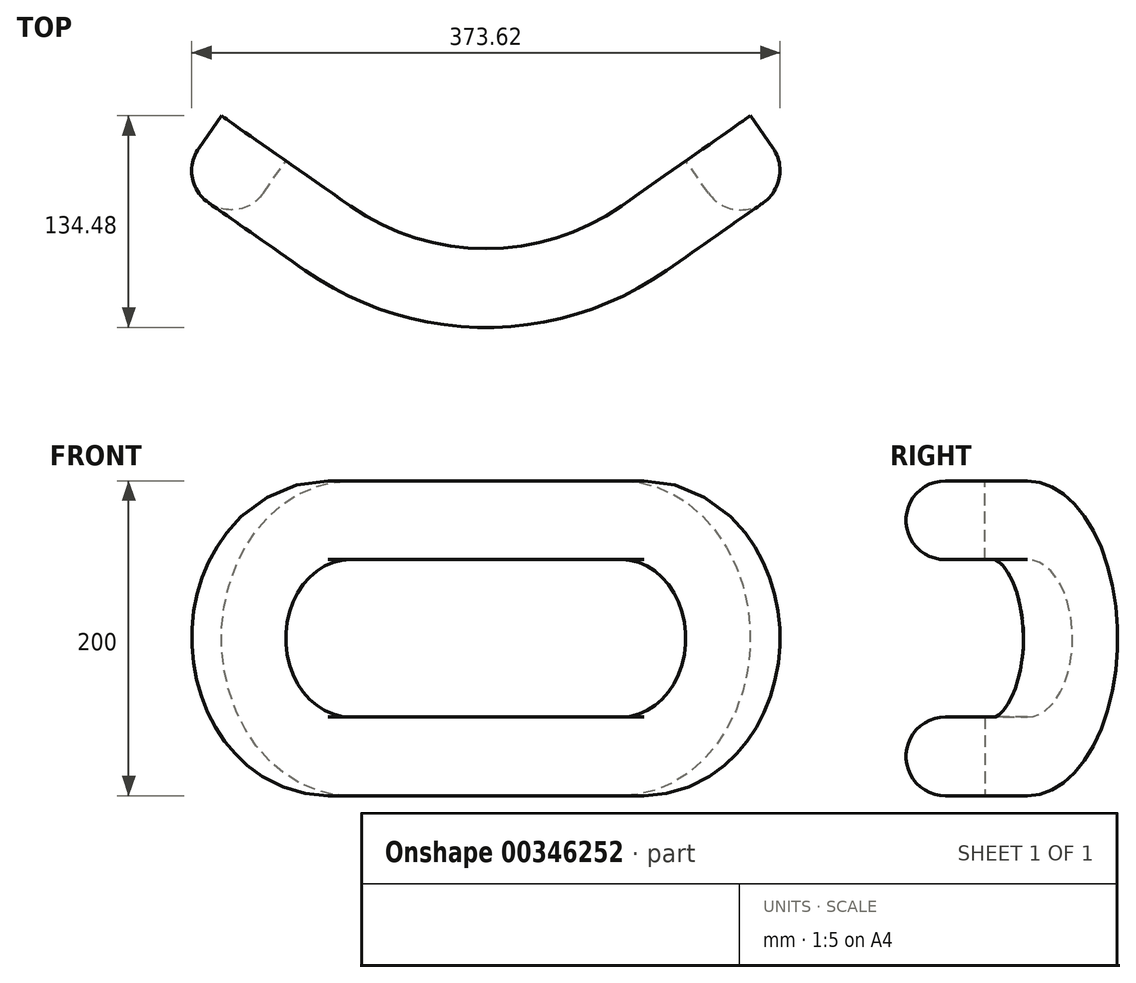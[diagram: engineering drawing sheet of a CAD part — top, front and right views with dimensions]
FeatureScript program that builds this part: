
annotation { "Feature Type Name" : "Feature", "Feature Type Description" : "" }
export const myFeature = defineFeature(function(context is Context, id is Id, definition is map)
    precondition{}
    {
        {
            var Q0;
            Q0=qCreatedBy(makeId("Top.planeOp"),FACE);
            var sketch = newSketch(context, id + "F0", { "sketchPlane" : qUnion([Q0])});
            skArc(sketch, "E0", {"start": v(-86.04, -122.87) * mm, "mid": v(0, -150) * mm, "end": v(86.04, -122.87) * mm});
            skLineSegment(sketch, "E1", {"start": v(0, 0) * mm, "end": v(-86.04, -122.87) * mm, "construction": true});
            skLineSegment(sketch, "E2.MirrorCS", {"start": v(0, 0) * mm, "end": v(86.04, -122.87) * mm, "construction": true});
            skLineSegment(sketch, "E3", {"start": v(-86.04, -122.87) * mm, "end": v(-212.34, -34.43) * mm});
            skLineSegment(sketch, "E4.MirrorCS", {"start": v(86.04, -122.87) * mm, "end": v(212.34, -34.43) * mm});
            skSolve(sketch);
        }
        {
            var Q0;
            Q0=sQuery(id+"F0.wireOp",EDGE,"E4.MirrorCS");
            var Q1;
            Q1=sQuery(id+"F0.wireOp",EDGE,"E0");
            var Q2;
            Q2=sQuery(id+"F0.wireOp",EDGE,"E3");
            extrude(context, id + "F1", {"bodyType" : ToolBodyType.SURFACE, "surfaceEntities" : qUnion([Q0, Q1, Q2]), "depth" : 50 * mm, "hasSecondDirection" : true, "secondDirectionOppositeDirection" : true, "secondDirectionDepth" : 50 * mm});
        }
        {
            var Q0;
            Q0=makeQuery(id+"F1.opExtrude","SWEPT_FACE",FACE,{"disambiguationData":[OSD([sQuery(id+"F0.wireOp",EDGE,"E3")])]});
            var sketch = newSketch(context, id + "F2", { "sketchPlane" : qUnion([Q0])});
            skArc(sketch, "E5", {"start": v(0, 50) * mm, "mid": v(-50, 0) * mm, "end": v(0, -50) * mm});
            skSolve(sketch);
        }
        {
            var Q0;
            Q0=makeQuery(id+"F1.opExtrude","SWEPT_FACE",FACE,{"disambiguationData":[OSD([sQuery(id+"F0.wireOp",EDGE,"E4.MirrorCS")])]});
            var sketch = newSketch(context, id + "F3", { "sketchPlane" : qUnion([Q0])});
            skArc(sketch, "E6", {"start": v(0, -50) * mm, "mid": v(50, 0) * mm, "end": v(0, 50) * mm});
            skSolve(sketch);
        }
        {
            var Q0;
            Q0=makeQuery(id+"F1.opExtrude","SWEPT_EDGE",EDGE,{"disambiguationData":[OSD([sQuery(id+"F0.wireOp",VERTEX,"E3.start")])]});
            var Q1;
            Q1=sQuery(id+"F2.wireOp",EDGE,"E5");
            cPlane(context, id + "F4", {"entities" : qUnion([Q0, Q1]), "cplaneType" : CPlaneType.LINE_ANGLE, "offset" : 25 * mm, "angle" : 0 * degree, "width" : 150 * mm, "height" : 150 * mm});
        }
        {
            var Q0;
            Q0=qCreatedBy(id+"F4.planeOp",FACE);
            var sketch = newSketch(context, id + "F5", { "sketchPlane" : qUnion([Q0])});
            skLineSegment(sketch, "E7.bottom", {"start": v(-150, 50) * mm, "end": v(-175, 50) * mm});
            skLineSegment(sketch, "E7.top", {"start": v(-150, 100) * mm, "end": v(-175, 100) * mm});
            skLineSegment(sketch, "E7.left", {"start": v(-150, 50) * mm, "end": v(-150, 100) * mm});
            skArc(sketch, "E8", {"start": v(-175, 100) * mm, "mid": v(-200, 75) * mm, "end": v(-175, 50) * mm});
            skPoint(sketch, "E8.centerSnap0", {"position": v(-175, 50) * mm});
            skPoint(sketch, "E8.centerSnap1", {"position": v(-150, 75) * mm});
            skPoint(sketch, "E9.orphan", {"position": v(-200, 50) * mm});
            skSolve(sketch);
        }
        {
            var Q0;
            Q0 = qSketchRegion(id + "F5", true);
            var Q1;
            Q1=sQuery(id+"F2.wireOp",EDGE,"E5");
            var Q2;
            Q2=makeQuery(id+"F1.opExtrude","CAP_EDGE",EDGE,{"disambiguationData":[OSD([sQuery(id+"F0.wireOp",EDGE,"E0")])],"isStart":true});
            var Q3;
            Q3=sQuery(id+"F3.wireOp",EDGE,"E6");
            var Q4;
            Q4=makeQuery(id+"F1.opExtrude","CAP_EDGE",EDGE,{"disambiguationData":[OSD([sQuery(id+"F0.wireOp",EDGE,"E0")])],"isStart":false});
            sweep(context, id + "F6", {"profiles" : qUnion([Q0]), "path" : qUnion([Q1, Q2, Q3, Q4])});
        }
    });
